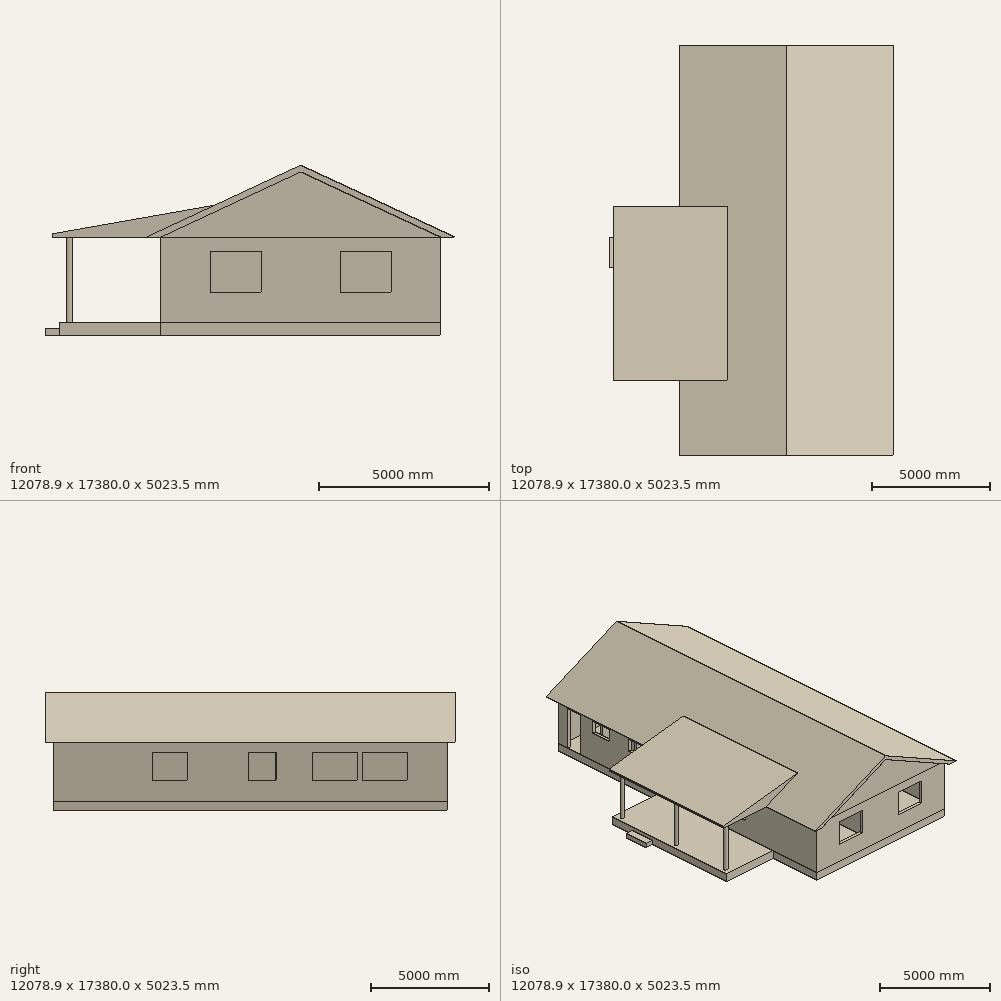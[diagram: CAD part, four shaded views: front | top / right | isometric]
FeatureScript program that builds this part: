
annotation { "Feature Type Name" : "Feature", "Feature Type Description" : "" }
export const myFeature = defineFeature(function(context is Context, id is Id, definition is map)
    precondition{}
    {
        {
            var Q0;
            Q0=qCreatedBy(makeId("Top.planeOp"),FACE);
            var sketch = newSketch(context, id + "F0", { "sketchPlane" : qUnion([Q0])});
            skLineSegment(sketch, "E0.bottom", {"start": v(-4125, 0) * mm, "end": v(4125, 0) * mm});
            skLineSegment(sketch, "E0.left", {"start": v(-4125, 0) * mm, "end": v(-4125, -9510) * mm});
            skLineSegment(sketch, "E0.right", {"start": v(4125, 0) * mm, "end": v(4125, -9510) * mm});
            skLineSegment(sketch, "E1.bottom", {"start": v(-3955, -200) * mm, "end": v(-195, -200) * mm});
            skLineSegment(sketch, "E1.top", {"start": v(-3955, -1700) * mm, "end": v(-195, -1700) * mm});
            skLineSegment(sketch, "E1.left", {"start": v(-3955, -200) * mm, "end": v(-3955, -1700) * mm});
            skLineSegment(sketch, "E1.right", {"start": v(-195, -200) * mm, "end": v(-195, -1700) * mm});
            skLineSegment(sketch, "E2.bottom", {"start": v(-3955, -1850) * mm, "end": v(-2105, -1850) * mm});
            skLineSegment(sketch, "E2.top", {"start": v(-3955, -3860) * mm, "end": v(-2105, -3860) * mm});
            skLineSegment(sketch, "E2.left", {"start": v(-3955, -1850) * mm, "end": v(-3955, -3860) * mm});
            skLineSegment(sketch, "E2.right", {"start": v(-2105, -1850) * mm, "end": v(-2105, -3860) * mm});
            skLineSegment(sketch, "E3.bottom", {"start": v(-1905, -1850) * mm, "end": v(-195, -1850) * mm});
            skLineSegment(sketch, "E3.top", {"start": v(-1905, -3860) * mm, "end": v(-195, -3860) * mm});
            skLineSegment(sketch, "E3.left", {"start": v(-1905, -1850) * mm, "end": v(-1905, -3860) * mm});
            skLineSegment(sketch, "E4.bottom", {"start": v(-3955, -3975) * mm, "end": v(-195, -3975) * mm});
            skLineSegment(sketch, "E4.top", {"start": v(-2825, -6245) * mm, "end": v(-195, -6245) * mm});
            skLineSegment(sketch, "E4.left", {"start": v(-3955, -3975) * mm, "end": v(-3955, -6245) * mm});
            skLineSegment(sketch, "E4.right", {"start": v(-195, -3975) * mm, "end": v(-195, -6245) * mm});
            skLineSegment(sketch, "E5.bottom", {"start": v(-2825, -7245) * mm, "end": v(-3955, -7245) * mm});
            skLineSegment(sketch, "E5.left", {"start": v(-2825, -7245) * mm, "end": v(-2825, -6245) * mm});
            skLineSegment(sketch, "E5.right", {"start": v(-3955, -7245) * mm, "end": v(-3955, -6245) * mm});
            skLineSegment(sketch, "E6.bottom", {"start": v(-3955, -9310) * mm, "end": v(-2825, -9310) * mm});
            skLineSegment(sketch, "E6.top", {"start": v(-3955, -7360) * mm, "end": v(-2825, -7360) * mm});
            skLineSegment(sketch, "E6.left", {"start": v(-3955, -9310) * mm, "end": v(-3955, -7360) * mm});
            skLineSegment(sketch, "E6.right", {"start": v(-2825, -9310) * mm, "end": v(-2825, -7360) * mm});
            skLineSegment(sketch, "E7.bottom", {"start": v(-2665, -6430) * mm, "end": v(-1545, -6430) * mm});
            skLineSegment(sketch, "E7.top", {"start": v(-2665, -7530) * mm, "end": v(-1545, -7530) * mm});
            skLineSegment(sketch, "E7.left", {"start": v(-2665, -6430) * mm, "end": v(-2665, -7530) * mm});
            skLineSegment(sketch, "E7.right", {"start": v(-1545, -6430) * mm, "end": v(-1545, -7530) * mm});
            skLineSegment(sketch, "E8.bottom", {"start": v(-45, -200) * mm, "end": v(3955, -200) * mm});
            skLineSegment(sketch, "E8.top", {"start": v(1905, -5800) * mm, "end": v(3955, -5800) * mm});
            skLineSegment(sketch, "E8.right", {"start": v(3955, -200) * mm, "end": v(3955, -5800) * mm});
            skLineSegment(sketch, "E9.bottom", {"start": v(3955, -9310) * mm, "end": v(955, -9310) * mm});
            skLineSegment(sketch, "E9.top", {"start": v(3955, -6490) * mm, "end": v(1905, -6490) * mm});
            skLineSegment(sketch, "E9.left", {"start": v(3955, -9310) * mm, "end": v(3955, -6490) * mm});
            skLineSegment(sketch, "E9.right", {"start": v(955, -9310) * mm, "end": v(955, -7290) * mm});
            skLineSegment(sketch, "E10.bottom", {"start": v(805, -9310) * mm, "end": v(-2665, -9310) * mm});
            skLineSegment(sketch, "E10.top", {"start": v(-1415, -7630) * mm, "end": v(-2665, -7630) * mm});
            skLineSegment(sketch, "E10.right", {"start": v(-2665, -9310) * mm, "end": v(-2665, -7630) * mm});
            skLineSegment(sketch, "E11.left", {"start": v(-1415, -6430) * mm, "end": v(-1415, -7630) * mm});
            skLineSegment(sketch, "E12", {"start": v(-2955, -3860) * mm, "end": v(-2955, -3330) * mm});
            skLineSegment(sketch, "E13", {"start": v(-2955, -3330) * mm, "end": v(-2105, -3330) * mm});
            skLineSegment(sketch, "E14", {"start": v(-195, -1850) * mm, "end": v(-195, -3860) * mm});
            skLineSegment(sketch, "E15", {"start": v(805, -9310) * mm, "end": v(805, -7290) * mm});
            skLineSegment(sketch, "E16", {"start": v(805, -7290) * mm, "end": v(955, -7290) * mm});
            skLineSegment(sketch, "E17", {"start": v(1905, -6490) * mm, "end": v(1905, -5800) * mm});
            skLineSegment(sketch, "E18", {"start": v(-1415, -6430) * mm, "end": v(-45, -6430) * mm});
            skLineSegment(sketch, "E19", {"start": v(-45, -6430) * mm, "end": v(-45, -200) * mm});
            skLineSegment(sketch, "E20", {"start": v(-4125, -9510) * mm, "end": v(4125, -9510) * mm});
            skLineSegment(sketch, "E21", {"start": v(-4125, -9510) * mm, "end": v(-4125, -16680) * mm});
            skLineSegment(sketch, "E22", {"start": v(-4125, -16680) * mm, "end": v(4125, -16680) * mm});
            skLineSegment(sketch, "E23", {"start": v(4125, -16680) * mm, "end": v(4125, -9510) * mm});
            skLineSegment(sketch, "E24", {"start": v(-3955, -9510) * mm, "end": v(-3955, -16510) * mm});
            skLineSegment(sketch, "E25", {"start": v(-3955, -16510) * mm, "end": v(3955, -16510) * mm});
            skLineSegment(sketch, "E26", {"start": v(3955, -16510) * mm, "end": v(3955, -9510) * mm});
            skLineSegment(sketch, "E27", {"start": v(-145, -9510) * mm, "end": v(-145, -16510) * mm});
            skLineSegment(sketch, "E28", {"start": v(-245, -16510) * mm, "end": v(-245, -9510) * mm});
            skLineSegment(sketch, "E29", {"start": v(-245, -12960) * mm, "end": v(-3955, -12960) * mm});
            skLineSegment(sketch, "E30", {"start": v(-3955, -12960) * mm, "end": v(-3955, -13060) * mm});
            skLineSegment(sketch, "E31", {"start": v(-245, -13060) * mm, "end": v(-3955, -13060) * mm});
            skSolve(sketch);
        }
        {
            var Q0;
            Q0=makeQuery(id+"F0.imprint","IMPRINT",FACE,{"disambiguationData":[TD([[makeQuery(id+"F0.imprint","IMPRINT",EDGE,{"derivedFrom":sQuery(id+"F0.wireOp",EDGE,"E0.bottom")}),-1.0]])]});
            var Q1;
            {var subQ3=sQuery(id+"F0.wireOp",EDGE,"E12");Q1=makeQuery(id+"F0.imprint","IMPRINT",FACE,{"disambiguationData":[TD([[makeQuery(id+"F0.imprint","IMPRINT",EDGE,{"derivedFrom":subQ3}),-1.0]])]});}
            var Q2;
            {var subQ4=sQuery(id+"F0.wireOp",EDGE,"E27");Q2=makeQuery(id+"F0.imprint","IMPRINT",FACE,{"disambiguationData":[TD([[makeQuery(id+"F0.imprint","IMPRINT",EDGE,{"derivedFrom":subQ4}),-1.0]])]});}
            var Q3;
            {var subQ2=sQuery(id+"F0.wireOp",EDGE,"E29");Q3=makeQuery(id+"F0.imprint","IMPRINT",FACE,{"disambiguationData":[TD([[makeQuery(id+"F0.imprint","IMPRINT",EDGE,{"derivedFrom":subQ2}),1.0]])]});}
            var Q4;
            {var subQ11=sQuery(id+"F0.wireOp",EDGE,"E21");Q4=makeQuery(id+"F0.imprint","IMPRINT",FACE,{"disambiguationData":[TD([[makeQuery(id+"F0.imprint","IMPRINT",EDGE,{"derivedFrom":subQ11}),1.0]])]});}
            extrude(context, id + "F1", {"entities" : qUnion([Q0, Q1, Q2, Q3, Q4]), "depth" : 2500 * mm, "offsetDistance" : 25 * mm});
        }
        {
            var Q0;
            Q0=makeQuery(id+"F1.opExtrude","CAP_FACE",FACE,{"disambiguationData":[OSD([sQuery(id+"F0.wireOp",EDGE,"E0.bottom"),sQuery(id+"F0.wireOp",EDGE,"E0.left"),sQuery(id+"F0.wireOp",EDGE,"E0.right"),sQuery(id+"F0.wireOp",EDGE,"E1.bottom"),sQuery(id+"F0.wireOp",EDGE,"E1.top"),sQuery(id+"F0.wireOp",EDGE,"E1.left"),sQuery(id+"F0.wireOp",EDGE,"E1.right"),sQuery(id+"F0.wireOp",EDGE,"E2.bottom"),sQuery(id+"F0.wireOp",EDGE,"E2.top"),sQuery(id+"F0.wireOp",EDGE,"E2.left"),sQuery(id+"F0.wireOp",EDGE,"E2.right"),sQuery(id+"F0.wireOp",EDGE,"E3.bottom"),sQuery(id+"F0.wireOp",EDGE,"E3.top"),sQuery(id+"F0.wireOp",EDGE,"E3.left"),sQuery(id+"F0.wireOp",EDGE,"E4.bottom"),sQuery(id+"F0.wireOp",EDGE,"E4.top"),sQuery(id+"F0.wireOp",EDGE,"E4.left"),sQuery(id+"F0.wireOp",EDGE,"E4.right"),sQuery(id+"F0.wireOp",EDGE,"E5.bottom"),sQuery(id+"F0.wireOp",EDGE,"E5.left"),sQuery(id+"F0.wireOp",EDGE,"E5.right"),sQuery(id+"F0.wireOp",EDGE,"E6.bottom"),sQuery(id+"F0.wireOp",EDGE,"E6.top"),sQuery(id+"F0.wireOp",EDGE,"E6.left"),sQuery(id+"F0.wireOp",EDGE,"E6.right"),sQuery(id+"F0.wireOp",EDGE,"E7.bottom"),sQuery(id+"F0.wireOp",EDGE,"E7.top"),sQuery(id+"F0.wireOp",EDGE,"E7.left"),sQuery(id+"F0.wireOp",EDGE,"E7.right"),sQuery(id+"F0.wireOp",EDGE,"E8.bottom"),sQuery(id+"F0.wireOp",EDGE,"E8.top"),sQuery(id+"F0.wireOp",EDGE,"E8.right"),sQuery(id+"F0.wireOp",EDGE,"E9.bottom"),sQuery(id+"F0.wireOp",EDGE,"E9.top"),sQuery(id+"F0.wireOp",EDGE,"E9.left"),sQuery(id+"F0.wireOp",EDGE,"E9.right"),sQuery(id+"F0.wireOp",EDGE,"E10.bottom"),sQuery(id+"F0.wireOp",EDGE,"E10.top"),sQuery(id+"F0.wireOp",EDGE,"E10.right"),sQuery(id+"F0.wireOp",EDGE,"E11.left"),sQuery(id+"F0.wireOp",EDGE,"E12"),sQuery(id+"F0.wireOp",EDGE,"E13"),sQuery(id+"F0.wireOp",EDGE,"E14"),sQuery(id+"F0.wireOp",EDGE,"E15"),sQuery(id+"F0.wireOp",EDGE,"E16"),sQuery(id+"F0.wireOp",EDGE,"E17"),sQuery(id+"F0.wireOp",EDGE,"E18"),sQuery(id+"F0.wireOp",EDGE,"E19"),sQuery(id+"F0.wireOp",EDGE,"E20"),sQuery(id+"F0.wireOp",EDGE,"E21"),sQuery(id+"F0.wireOp",EDGE,"E22"),sQuery(id+"F0.wireOp",EDGE,"E23"),sQuery(id+"F0.wireOp",EDGE,"E24"),sQuery(id+"F0.wireOp",EDGE,"E25"),sQuery(id+"F0.wireOp",EDGE,"E26"),sQuery(id+"F0.wireOp",EDGE,"E27"),sQuery(id+"F0.wireOp",EDGE,"E28"),sQuery(id+"F0.wireOp",EDGE,"E29"),sQuery(id+"F0.wireOp",EDGE,"E31")])],"isStart":false});
            var sketch = newSketch(context, id + "F2", { "sketchPlane" : qUnion([Q0])});
            skLineSegment(sketch, "E32", {"start": v(-95, -9310) * mm, "end": v(-95, -9510) * mm});
            skLineSegment(sketch, "E33", {"start": v(-95, -9510) * mm, "end": v(755, -9510) * mm});
            skLineSegment(sketch, "E34", {"start": v(755, -9510) * mm, "end": v(755, -9310) * mm});
            skLineSegment(sketch, "E35", {"start": v(-345, -9310) * mm, "end": v(-345, -9510) * mm});
            skLineSegment(sketch, "E36", {"start": v(-345, -9510) * mm, "end": v(-1195, -9510) * mm});
            skLineSegment(sketch, "E37", {"start": v(-1195, -9510) * mm, "end": v(-1195, -9310) * mm});
            skLineSegment(sketch, "E38", {"start": v(-2665, -7930) * mm, "end": v(-2825, -7930) * mm});
            skLineSegment(sketch, "E39", {"start": v(-2825, -7930) * mm, "end": v(-2825, -8810) * mm});
            skLineSegment(sketch, "E40", {"start": v(-2825, -8810) * mm, "end": v(-2665, -8810) * mm});
            skLineSegment(sketch, "E41", {"start": v(-2215, -7530) * mm, "end": v(-2215, -7630) * mm});
            skLineSegment(sketch, "E42", {"start": v(-2215, -7630) * mm, "end": v(-1565, -7630) * mm});
            skLineSegment(sketch, "E43", {"start": v(-1565, -7630) * mm, "end": v(-1565, -7530) * mm});
            skLineSegment(sketch, "E44", {"start": v(-3755, -7245) * mm, "end": v(-3755, -7360) * mm});
            skLineSegment(sketch, "E45", {"start": v(-3755, -7360) * mm, "end": v(-2905, -7360) * mm});
            skLineSegment(sketch, "E46", {"start": v(-2905, -7360) * mm, "end": v(-2905, -7245) * mm});
            skLineSegment(sketch, "E47", {"start": v(-205, -3860) * mm, "end": v(-205, -3975) * mm});
            skLineSegment(sketch, "E48", {"start": v(-205, -3975) * mm, "end": v(-1075, -3975) * mm});
            skLineSegment(sketch, "E49", {"start": v(-1075, -3975) * mm, "end": v(-1075, -3860) * mm});
            skLineSegment(sketch, "E50", {"start": v(-3935, -3860) * mm, "end": v(-3935, -3975) * mm});
            skLineSegment(sketch, "E51", {"start": v(-3935, -3975) * mm, "end": v(-3055, -3975) * mm});
            skLineSegment(sketch, "E52", {"start": v(-3055, -3975) * mm, "end": v(-3055, -1850) * mm});
            skLineSegment(sketch, "E53", {"start": v(-3935, -1700) * mm, "end": v(-3935, -1850) * mm});
            skLineSegment(sketch, "E54", {"start": v(-3935, -1850) * mm, "end": v(-3135, -1850) * mm});
            skLineSegment(sketch, "E55", {"start": v(-3135, -1850) * mm, "end": v(-3135, -1700) * mm});
            skLineSegment(sketch, "E56", {"start": v(-4125, -7980) * mm, "end": v(-3955, -7980) * mm});
            skLineSegment(sketch, "E57", {"start": v(-3955, -7980) * mm, "end": v(-3955, -8860) * mm});
            skLineSegment(sketch, "E58", {"start": v(-3955, -8860) * mm, "end": v(-4125, -8860) * mm});
            skLineSegment(sketch, "E59", {"start": v(-3955, -600) * mm, "end": v(-4125, -600) * mm});
            skLineSegment(sketch, "E60", {"start": v(-4125, -600) * mm, "end": v(-4125, -1450) * mm});
            skLineSegment(sketch, "E61", {"start": v(-4125, -1450) * mm, "end": v(-3955, -1450) * mm});
            skLineSegment(sketch, "E62", {"start": v(-245, -13160) * mm, "end": v(-145, -13160) * mm});
            skLineSegment(sketch, "E63", {"start": v(-145, -13160) * mm, "end": v(-145, -14010) * mm});
            skLineSegment(sketch, "E64", {"start": v(-145, -14010) * mm, "end": v(-245, -14010) * mm});
            skSolve(sketch);
        }
        {
            var Q0;
            {var subQ0=sQuery(id+"F2.wireOp",EDGE,"E59");Q0=makeQuery(id+"F2.imprint","IMPRINT",FACE,{"disambiguationData":[TD([[makeQuery(id+"F2.imprint","IMPRINT",EDGE,{"derivedFrom":subQ0}),1.0]])]});}
            var Q1;
            {var subQ0=sQuery(id+"F2.wireOp",EDGE,"E53");Q1=makeQuery(id+"F2.imprint","IMPRINT",FACE,{"disambiguationData":[TD([[makeQuery(id+"F2.imprint","IMPRINT",EDGE,{"derivedFrom":subQ0}),1.0]])]});}
            var Q2;
            {var subQ0=sQuery(id+"F2.wireOp",EDGE,"E50");Q2=makeQuery(id+"F2.imprint","IMPRINT",FACE,{"disambiguationData":[TD([[makeQuery(id+"F2.imprint","IMPRINT",EDGE,{"derivedFrom":subQ0}),1.0]])]});}
            var Q3;
            {var subQ0=sQuery(id+"F2.wireOp",EDGE,"E47");Q3=makeQuery(id+"F2.imprint","IMPRINT",FACE,{"disambiguationData":[TD([[makeQuery(id+"F2.imprint","IMPRINT",EDGE,{"derivedFrom":subQ0}),-1.0]])]});}
            var Q4;
            {var subQ0=sQuery(id+"F2.wireOp",EDGE,"E44");Q4=makeQuery(id+"F2.imprint","IMPRINT",FACE,{"disambiguationData":[TD([[makeQuery(id+"F2.imprint","IMPRINT",EDGE,{"derivedFrom":subQ0}),1.0]])]});}
            var Q5;
            {var subQ0=sQuery(id+"F2.wireOp",EDGE,"E56");Q5=makeQuery(id+"F2.imprint","IMPRINT",FACE,{"disambiguationData":[TD([[makeQuery(id+"F2.imprint","IMPRINT",EDGE,{"derivedFrom":subQ0}),-1.0]])]});}
            var Q6;
            {var subQ0=sQuery(id+"F2.wireOp",EDGE,"E41");Q6=makeQuery(id+"F2.imprint","IMPRINT",FACE,{"disambiguationData":[TD([[makeQuery(id+"F2.imprint","IMPRINT",EDGE,{"derivedFrom":subQ0}),1.0]])]});}
            var Q7;
            {var subQ0=sQuery(id+"F2.wireOp",EDGE,"E38");Q7=makeQuery(id+"F2.imprint","IMPRINT",FACE,{"disambiguationData":[TD([[makeQuery(id+"F2.imprint","IMPRINT",EDGE,{"derivedFrom":subQ0}),1.0]])]});}
            var Q8;
            {var subQ0=sQuery(id+"F2.wireOp",EDGE,"E35");Q8=makeQuery(id+"F2.imprint","IMPRINT",FACE,{"disambiguationData":[TD([[makeQuery(id+"F2.imprint","IMPRINT",EDGE,{"derivedFrom":subQ0}),-1.0]])]});}
            var Q9;
            {var subQ0=sQuery(id+"F2.wireOp",EDGE,"E32");Q9=makeQuery(id+"F2.imprint","IMPRINT",FACE,{"disambiguationData":[TD([[makeQuery(id+"F2.imprint","IMPRINT",EDGE,{"derivedFrom":subQ0}),1.0]])]});}
            var Q10;
            {var subQ0=sQuery(id+"F2.wireOp",EDGE,"DsypGBD1-VUyX-LvVu-Ju5p-gGMJGe04lbca");Q10=makeQuery(id+"F2.imprint","IMPRINT",FACE,{"disambiguationData":[TD([[makeQuery(id+"F2.imprint","IMPRINT",EDGE,{"derivedFrom":subQ0}),1.0]])]});}
            var Q11;
            {var subQ0=sQuery(id+"F2.wireOp",EDGE,"xUU9sHKB-wWJu-vvyQ-Y27K-SafOuSSaSPCu");Q11=makeQuery(id+"F2.imprint","IMPRINT",FACE,{"disambiguationData":[TD([[makeQuery(id+"F2.imprint","IMPRINT",EDGE,{"derivedFrom":subQ0}),1.0]])]});}
            var Q12;
            {var subQ0=sQuery(id+"F2.wireOp",EDGE,"gtOgTZcF-iGIu-P8De-4s3f-iU6d5bzWKqcu");Q12=makeQuery(id+"F2.imprint","IMPRINT",FACE,{"disambiguationData":[TD([[makeQuery(id+"F2.imprint","IMPRINT",EDGE,{"derivedFrom":subQ0}),-1.0]])]});}
            var Q13;
            {var subQ0=sQuery(id+"F2.wireOp",EDGE,"w5LqMJMD-BTsf-lrcy-2qe3-qbSku6zuDei2");Q13=makeQuery(id+"F2.imprint","IMPRINT",FACE,{"disambiguationData":[TD([[makeQuery(id+"F2.imprint","IMPRINT",EDGE,{"derivedFrom":subQ0}),1.0]])]});}
            var Q14;
            {var subQ0=sQuery(id+"F2.wireOp",EDGE,"gPe3p3GD-z5Sc-NsmL-BG3g-iFZIMeydH4XN");Q14=makeQuery(id+"F2.imprint","IMPRINT",FACE,{"disambiguationData":[TD([[makeQuery(id+"F2.imprint","IMPRINT",EDGE,{"derivedFrom":subQ0}),1.0]])]});}
            var Q15;
            {var subQ0=sQuery(id+"F2.wireOp",EDGE,"yB4fgNzf-4WXd-bTIO-ROpB-tO7Q6PLyojeI");Q15=makeQuery(id+"F2.imprint","IMPRINT",FACE,{"disambiguationData":[TD([[makeQuery(id+"F2.imprint","IMPRINT",EDGE,{"derivedFrom":subQ0}),-1.0]])]});}
            var Q16;
            {var subQ0=sQuery(id+"F2.wireOp",EDGE,"iTkjHG0i-oWPG-WNHC-gP18-lA7tzI3W6FOF");Q16=makeQuery(id+"F2.imprint","IMPRINT",FACE,{"disambiguationData":[TD([[makeQuery(id+"F2.imprint","IMPRINT",EDGE,{"derivedFrom":subQ0}),-1.0]])]});}
            var Q17;
            {var subQ0=sQuery(id+"F2.wireOp",EDGE,"AnUvtcCU-d7Ku-vRum-K7dT-Ix1SRXOT5qH1");Q17=makeQuery(id+"F2.imprint","IMPRINT",FACE,{"disambiguationData":[TD([[makeQuery(id+"F2.imprint","IMPRINT",EDGE,{"derivedFrom":subQ0}),-1.0]])]});}
            var Q18;
            {var subQ0=sQuery(id+"F2.wireOp",EDGE,"E62");Q18=makeQuery(id+"F2.imprint","IMPRINT",FACE,{"disambiguationData":[TD([[makeQuery(id+"F2.imprint","IMPRINT",EDGE,{"derivedFrom":subQ0}),-1.0]])]});}
            extrude(context, id + "F3", {"entities" : qUnion([Q0, Q1, Q2, Q3, Q4, Q5, Q6, Q7, Q8, Q9, Q10, Q11, Q12, Q13, Q14, Q15, Q16, Q17, Q18]), "operationType" : NewBodyOperationType.REMOVE, "endBound" : BoundingType.UP_TO_NEXT, "oppositeDirection" : true, "depth" : 2200 * mm, "hasSecondDirection" : true, "secondDirectionOppositeDirection" : true, "secondDirectionDepth" : 400 * mm});
        }
        {
            var Q0;
            Q0=qCreatedBy(makeId("Top.planeOp"),FACE);
            var sketch = newSketch(context, id + "F4", { "sketchPlane" : qUnion([Q0])});
            skLineSegment(sketch, "E65.bottom", {"start": v(4125, -16680) * mm, "end": v(-4125, -16680) * mm});
            skLineSegment(sketch, "E65.top", {"start": v(4125, 0) * mm, "end": v(-4125, 0) * mm});
            skLineSegment(sketch, "E65.left", {"start": v(4125, -16680) * mm, "end": v(4125, 0) * mm});
            skLineSegment(sketch, "E65.right", {"start": v(-4125, -16680) * mm, "end": v(-4125, 0) * mm});
            skSolve(sketch);
        }
        {
            var Q0;
            Q0=qSketchRegion(id+"F4",true);
            extrude(context, id + "F5", {"entities" : qUnion([Q0]), "oppositeDirection" : true, "depth" : 400 * mm, "offsetDistance" : 25 * mm});
        }
        {
            var Q0;
            Q0=makeQuery(id+"F1.opExtrude","SWEPT_FACE",FACE,{"disambiguationData":[OSD([sQuery(id+"F0.wireOp",EDGE,"E0.left"),sQuery(id+"F0.wireOp",EDGE,"E21")])]});
            var sketch = newSketch(context, id + "F6", { "sketchPlane" : qUnion([Q0])});
            skLineSegment(sketch, "E66.bottom", {"start": v(2210, 2100) * mm, "end": v(3310, 2100) * mm});
            skLineSegment(sketch, "E66.top", {"start": v(2210, 1450) * mm, "end": v(3310, 1450) * mm});
            skLineSegment(sketch, "E66.left", {"start": v(2210, 2100) * mm, "end": v(2210, 1450) * mm});
            skLineSegment(sketch, "E66.right", {"start": v(3310, 2100) * mm, "end": v(3310, 1450) * mm});
            skLineSegment(sketch, "E67.bottom", {"start": v(5895, 2100) * mm, "end": v(4545, 2100) * mm});
            skLineSegment(sketch, "E67.top", {"start": v(5895, 1450) * mm, "end": v(4545, 1450) * mm});
            skLineSegment(sketch, "E67.left", {"start": v(5895, 2100) * mm, "end": v(5895, 1450) * mm});
            skLineSegment(sketch, "E67.right", {"start": v(4545, 2100) * mm, "end": v(4545, 1450) * mm});
            skLineSegment(sketch, "E68.bottom", {"start": v(7740, 2050) * mm, "end": v(7390, 2050) * mm});
            skLineSegment(sketch, "E68.top", {"start": v(7740, 850) * mm, "end": v(7390, 850) * mm});
            skLineSegment(sketch, "E68.left", {"start": v(7740, 2050) * mm, "end": v(7740, 850) * mm});
            skLineSegment(sketch, "E68.right", {"start": v(7390, 2050) * mm, "end": v(7390, 850) * mm});
            skLineSegment(sketch, "E69.bottom", {"start": v(10610, 2080) * mm, "end": v(12110, 2080) * mm});
            skLineSegment(sketch, "E69.top", {"start": v(10610, 880) * mm, "end": v(12110, 880) * mm});
            skLineSegment(sketch, "E69.left", {"start": v(10610, 2080) * mm, "end": v(10610, 880) * mm});
            skLineSegment(sketch, "E69.right", {"start": v(12110, 2080) * mm, "end": v(12110, 880) * mm});
            skSolve(sketch);
        }
        {
            var Q0;
            Q0=makeQuery(id+"F1.opExtrude","SWEPT_FACE",FACE,{"disambiguationData":[OSD([sQuery(id+"F0.wireOp",EDGE,"E0.bottom")])]});
            var sketch = newSketch(context, id + "F7", { "sketchPlane" : qUnion([Q0])});
            skLineSegment(sketch, "E70.bottom", {"start": v(1255, 2100) * mm, "end": v(2555, 2100) * mm});
            skLineSegment(sketch, "E70.top", {"start": v(1255, 1450) * mm, "end": v(2555, 1450) * mm});
            skLineSegment(sketch, "E70.left", {"start": v(1255, 2100) * mm, "end": v(1255, 1450) * mm});
            skLineSegment(sketch, "E70.right", {"start": v(2555, 2100) * mm, "end": v(2555, 1450) * mm});
            skSolve(sketch);
        }
        {
            var Q0;
            Q0=makeQuery(id+"F1.opExtrude","SWEPT_FACE",FACE,{"disambiguationData":[OSD([sQuery(id+"F0.wireOp",EDGE,"E0.right"),sQuery(id+"F0.wireOp",EDGE,"E23")])]});
            var sketch = newSketch(context, id + "F8", { "sketchPlane" : qUnion([Q0])});
            skLineSegment(sketch, "E71.bottom", {"start": v(-8440, 2080) * mm, "end": v(-7240, 2080) * mm});
            skLineSegment(sketch, "E71.top", {"start": v(-8440, 880) * mm, "end": v(-7240, 880) * mm});
            skLineSegment(sketch, "E71.left", {"start": v(-8440, 2080) * mm, "end": v(-8440, 880) * mm});
            skLineSegment(sketch, "E71.right", {"start": v(-7240, 2080) * mm, "end": v(-7240, 880) * mm});
            skLineSegment(sketch, "E72.bottom", {"start": v(-5700, 2080) * mm, "end": v(-3800, 2080) * mm});
            skLineSegment(sketch, "E72.top", {"start": v(-5700, 880) * mm, "end": v(-3800, 880) * mm});
            skLineSegment(sketch, "E72.left", {"start": v(-5700, 2080) * mm, "end": v(-5700, 880) * mm});
            skLineSegment(sketch, "E72.right", {"start": v(-3800, 2080) * mm, "end": v(-3800, 880) * mm});
            skLineSegment(sketch, "E73.bottom", {"start": v(-3600, 2080) * mm, "end": v(-1700, 2080) * mm});
            skLineSegment(sketch, "E73.top", {"start": v(-3600, 880) * mm, "end": v(-1700, 880) * mm});
            skLineSegment(sketch, "E73.left", {"start": v(-3600, 2080) * mm, "end": v(-3600, 880) * mm});
            skLineSegment(sketch, "E73.right", {"start": v(-1700, 2080) * mm, "end": v(-1700, 880) * mm});
            skLineSegment(sketch, "E74.bottom", {"start": v(-11010, 2080) * mm, "end": v(-12510, 2080) * mm});
            skLineSegment(sketch, "E74.top", {"start": v(-11010, 880) * mm, "end": v(-12510, 880) * mm});
            skLineSegment(sketch, "E74.left", {"start": v(-11010, 2080) * mm, "end": v(-11010, 880) * mm});
            skLineSegment(sketch, "E74.right", {"start": v(-12510, 2080) * mm, "end": v(-12510, 880) * mm});
            skLineSegment(sketch, "E75.bottom", {"start": v(-14010, 2080) * mm, "end": v(-15510, 2080) * mm});
            skLineSegment(sketch, "E75.top", {"start": v(-14010, 880) * mm, "end": v(-15510, 880) * mm});
            skLineSegment(sketch, "E75.left", {"start": v(-14010, 2080) * mm, "end": v(-14010, 880) * mm});
            skLineSegment(sketch, "E75.right", {"start": v(-15510, 2080) * mm, "end": v(-15510, 880) * mm});
            skSolve(sketch);
        }
        {
            var Q0;
            Q0=makeQuery(id+"F1.opExtrude","SWEPT_FACE",FACE,{"disambiguationData":[OSD([sQuery(id+"F0.wireOp",EDGE,"E22")])]});
            var sketch = newSketch(context, id + "F9", { "sketchPlane" : qUnion([Q0])});
            skLineSegment(sketch, "E76.bottom", {"start": v(-2655, 2080) * mm, "end": v(-1155, 2080) * mm});
            skLineSegment(sketch, "E76.top", {"start": v(-2655, 880) * mm, "end": v(-1155, 880) * mm});
            skLineSegment(sketch, "E76.left", {"start": v(-2655, 2080) * mm, "end": v(-2655, 880) * mm});
            skLineSegment(sketch, "E76.right", {"start": v(-1155, 2080) * mm, "end": v(-1155, 880) * mm});
            skLineSegment(sketch, "E77.bottom", {"start": v(2655, 2080) * mm, "end": v(1155, 2080) * mm});
            skLineSegment(sketch, "E77.top", {"start": v(2655, 880) * mm, "end": v(1155, 880) * mm});
            skLineSegment(sketch, "E77.left", {"start": v(2655, 2080) * mm, "end": v(2655, 880) * mm});
            skLineSegment(sketch, "E77.right", {"start": v(1155, 2080) * mm, "end": v(1155, 880) * mm});
            skSolve(sketch);
        }
        {
            var Q0;
            Q0 = qSketchRegion(id + "F6", true);
            extrude(context, id + "F10", {"entities" : qUnion([Q0]), "operationType" : NewBodyOperationType.REMOVE, "endBound" : BoundingType.UP_TO_NEXT, "oppositeDirection" : true, "depth" : 25 * mm, "offsetDistance" : 25 * mm});
        }
        {
            var Q0;
            Q0 = qSketchRegion(id + "F7", true);
            extrude(context, id + "F11", {"entities" : qUnion([Q0]), "operationType" : NewBodyOperationType.REMOVE, "endBound" : BoundingType.UP_TO_NEXT, "oppositeDirection" : true, "depth" : 25 * mm, "offsetDistance" : 25 * mm});
        }
        {
            var Q0;
            Q0=makeQuery(id+"F8.imprint","IMPRINT",FACE,{"disambiguationData":[TD([[makeQuery(id+"F8.imprint","IMPRINT",EDGE,{"derivedFrom":sQuery(id+"F8.wireOp",EDGE,"E71.bottom")}),-1.0]])]});
            var Q1;
            Q1=makeQuery(id+"F8.imprint","IMPRINT",FACE,{"disambiguationData":[TD([[makeQuery(id+"F8.imprint","IMPRINT",EDGE,{"derivedFrom":sQuery(id+"F8.wireOp",EDGE,"E72.bottom")}),-1.0]])]});
            var Q2;
            Q2=makeQuery(id+"F8.imprint","IMPRINT",FACE,{"disambiguationData":[TD([[makeQuery(id+"F8.imprint","IMPRINT",EDGE,{"derivedFrom":sQuery(id+"F8.wireOp",EDGE,"E73.bottom")}),-1.0]])]});
            var Q3;
            Q3=makeQuery(id+"F8.imprint","IMPRINT",FACE,{"disambiguationData":[TD([[makeQuery(id+"F8.imprint","IMPRINT",EDGE,{"derivedFrom":sQuery(id+"F8.wireOp",EDGE,"E74.bottom")}),1.0]])]});
            extrude(context, id + "F12", {"entities" : qUnion([Q0, Q1, Q2, Q3]), "operationType" : NewBodyOperationType.REMOVE, "endBound" : BoundingType.UP_TO_NEXT, "oppositeDirection" : true, "depth" : 25 * mm, "offsetDistance" : 25 * mm});
        }
        {
            var Q0;
            Q0 = qSketchRegion(id + "F9", true);
            extrude(context, id + "F13", {"entities" : qUnion([Q0]), "operationType" : NewBodyOperationType.REMOVE, "endBound" : BoundingType.UP_TO_NEXT, "oppositeDirection" : true, "depth" : 25 * mm, "offsetDistance" : 25 * mm});
        }
        {
            var Q0;
            Q0=makeQuery(id+"F1.opExtrude","SWEPT_FACE",FACE,{"disambiguationData":[OSD([sQuery(id+"F0.wireOp",EDGE,"E22")])]});
            var sketch = newSketch(context, id + "F14", { "sketchPlane" : qUnion([Q0])});
            skLineSegment(sketch, "E78", {"start": v(4125, 2500) * mm, "end": v(-4125, 2500) * mm});
            skLineSegment(sketch, "E79", {"start": v(-4125, 2500) * mm, "end": v(0, 4423.52) * mm});
            skPoint(sketch, "E79.endSnap0", {"position": v(0, 2500) * mm});
            skLineSegment(sketch, "E80", {"start": v(0, 4423.52) * mm, "end": v(4125, 2500) * mm});
            skSolve(sketch);
        }
        {
            var Q0;
            Q0 = qSketchRegion(id + "F14", true);
            var Q1;
            Q1=makeQuery(id+"F1.opExtrude","SWEPT_FACE",FACE,{"disambiguationData":[OSD([sQuery(id+"F0.wireOp",EDGE,"E0.bottom")])]});
            extrude(context, id + "F15", {"entities" : qUnion([Q0]), "endBound" : BoundingType.UP_TO_SURFACE, "oppositeDirection" : true, "depth" : 25 * mm, "endBoundEntityFace" : qUnion([Q1]), "offsetDistance" : 350 * mm, "offsetOppositeDirection" : true});
        }
        {
            var Q0;
            Q0=makeQuery(id+"F15.opExtrude","CAP_FACE",FACE,{"disambiguationData":[OSD([sQuery(id+"F14.wireOp",EDGE,"E78"),sQuery(id+"F14.wireOp",EDGE,"E79"),sQuery(id+"F14.wireOp",EDGE,"E80")])],"isStart":true});
            var sketch = newSketch(context, id + "F16", { "sketchPlane" : qUnion([Q0])});
            skLineSegment(sketch, "E81", {"start": v(-4553.9, 2500) * mm, "end": v(0, 4623.52) * mm});
            skLineSegment(sketch, "E82", {"start": v(0, 4623.52) * mm, "end": v(4553.9, 2500) * mm});
            skLineSegment(sketch, "E83", {"start": v(4553.9, 2500) * mm, "end": v(4125, 2500) * mm});
            skLineSegment(sketch, "E84", {"start": v(-4553.9, 2500) * mm, "end": v(-4125, 2500) * mm});
            skSolve(sketch);
        }
        {
            var Q0;
            Q0=makeQuery(id+"F16.imprint","IMPRINT",FACE,{"disambiguationData":[TD([[makeQuery(id+"F16.imprint","IMPRINT",EDGE,{"derivedFrom":sQuery(id+"F16.wireOp",EDGE,"E81")}),-1.0]])]});
            var Q1;
            Q1=makeQuery(id+"F15.opExtrude","CAP_FACE",FACE,{"disambiguationData":[OSD([sQuery(id+"F14.wireOp",EDGE,"E78"),sQuery(id+"F14.wireOp",EDGE,"E79"),sQuery(id+"F14.wireOp",EDGE,"E80")])],"isStart":false});
            extrude(context, id + "F17", {"entities" : qUnion([Q0]), "endBound" : BoundingType.UP_TO_SURFACE, "oppositeDirection" : true, "depth" : 9360 * mm, "endBoundEntityFace" : qUnion([Q1]), "hasOffset" : true, "offsetDistance" : 350 * mm, "offsetOppositeDirection" : true, "hasSecondDirection" : true, "secondDirectionOppositeDirection" : false, "secondDirectionDepth" : 350 * mm});
        }
        {
            var Q0;
            Q0=makeQuery(id+"F5.opExtrude","SWEPT_FACE",FACE,{"disambiguationData":[OSD([sQuery(id+"F4.wireOp",EDGE,"E65.right")])]});
            var sketch = newSketch(context, id + "F18", { "sketchPlane" : qUnion([Q0])});
            skLineSegment(sketch, "E85.bottom", {"start": v(6480, 0) * mm, "end": v(13860, 0) * mm});
            skLineSegment(sketch, "E85.top", {"start": v(6480, -400) * mm, "end": v(13860, -400) * mm});
            skLineSegment(sketch, "E85.left", {"start": v(6480, 0) * mm, "end": v(6480, -400) * mm});
            skLineSegment(sketch, "E85.right", {"start": v(13860, 0) * mm, "end": v(13860, -400) * mm});
            skSolve(sketch);
        }
        {
            var Q0;
            Q0 = qSketchRegion(id + "F18", true);
            extrude(context, id + "F19", {"entities" : qUnion([Q0]), "depth" : 3000 * mm, "offsetDistance" : 25 * mm});
        }
        {
            var Q0;
            Q0=makeQuery(id+"F19.opExtrude","CAP_FACE",FACE,{"disambiguationData":[OSD([sQuery(id+"F18.wireOp",EDGE,"E85.bottom"),sQuery(id+"F18.wireOp",EDGE,"E85.top"),sQuery(id+"F18.wireOp",EDGE,"E85.left"),sQuery(id+"F18.wireOp",EDGE,"E85.right")])],"isStart":false});
            var sketch = newSketch(context, id + "F20", { "sketchPlane" : qUnion([Q0])});
            skLineSegment(sketch, "E86", {"start": v(7780, -400) * mm, "end": v(7780, -180) * mm});
            skLineSegment(sketch, "E87", {"start": v(7780, -180) * mm, "end": v(9060, -180) * mm});
            skLineSegment(sketch, "E88", {"start": v(9060, -180) * mm, "end": v(9060, -400) * mm});
            skSolve(sketch);
        }
        {
            var Q0;
            {var subQ0=sQuery(id+"F20.wireOp",EDGE,"E86");Q0=makeQuery(id+"F20.imprint","IMPRINT",FACE,{"disambiguationData":[TD([[makeQuery(id+"F20.imprint","IMPRINT",EDGE,{"derivedFrom":subQ0}),-1.0]])]});}
            extrude(context, id + "F21", {"entities" : qUnion([Q0]), "operationType" : NewBodyOperationType.ADD, "depth" : 400 * mm, "offsetDistance" : 25 * mm});
        }
        {
            var Q0;
            Q0=makeQuery(id+"F19.opExtrude","SWEPT_FACE",FACE,{"disambiguationData":[OSD([sQuery(id+"F18.wireOp",EDGE,"E85.bottom")])]});
            var sketch = newSketch(context, id + "F22", { "sketchPlane" : qUnion([Q0])});
            skCircle(sketch, "E89", {"center": v(-6820, -6830) * mm, "radius": 100 * mm});
            skCircle(sketch, "E90", {"center": v(-6820, -13510) * mm, "radius": 100 * mm});
            skCircle(sketch, "E91", {"center": v(-6820, -10330) * mm, "radius": 100 * mm});
            skSolve(sketch);
        }
        {
            var Q0;
            Q0 = qSketchRegion(id + "F22", true);
            extrude(context, id + "F23", {"entities" : qUnion([Q0]), "operationType" : NewBodyOperationType.ADD, "depth" : 2500 * mm, "offsetDistance" : 25 * mm});
        }
        {
            var Q0;
            Q0=makeQuery(id+"F19.opExtrude","SWEPT_FACE",FACE,{"disambiguationData":[OSD([sQuery(id+"F18.wireOp",EDGE,"E85.right")])]});
            var sketch = newSketch(context, id + "F24", { "sketchPlane" : qUnion([Q0])});
            skLineSegment(sketch, "E92", {"start": v(-2518.9, 2500) * mm, "end": v(-7325, 2500) * mm});
            skLineSegment(sketch, "E93", {"start": v(-7325, 2500) * mm, "end": v(-7325, 2600) * mm});
            skLineSegment(sketch, "E94", {"start": v(-7325, 2600) * mm, "end": v(-2518.9, 3448.94) * mm});
            skLineSegment(sketch, "E95", {"start": v(-2518.9, 3448.94) * mm, "end": v(-2518.9, 2500) * mm});
            skSolve(sketch);
        }
        {
            var Q0;
            Q0=makeQuery(id+"F24.imprint","IMPRINT",FACE,{"disambiguationData":[TD([[makeQuery(id+"F24.imprint","IMPRINT",EDGE,{"derivedFrom":sQuery(id+"F24.wireOp",EDGE,"E92")}),-1.0]])]});
            var Q1;
            Q1=makeQuery(id+"F19.opExtrude","SWEPT_FACE",FACE,{"disambiguationData":[OSD([sQuery(id+"F18.wireOp",EDGE,"E85.left")])]});
            extrude(context, id + "F25", {"entities" : qUnion([Q0]), "endBound" : BoundingType.UP_TO_SURFACE, "oppositeDirection" : true, "depth" : 25 * mm, "endBoundEntityFace" : qUnion([Q1]), "offsetDistance" : 25 * mm});
        }
    });
